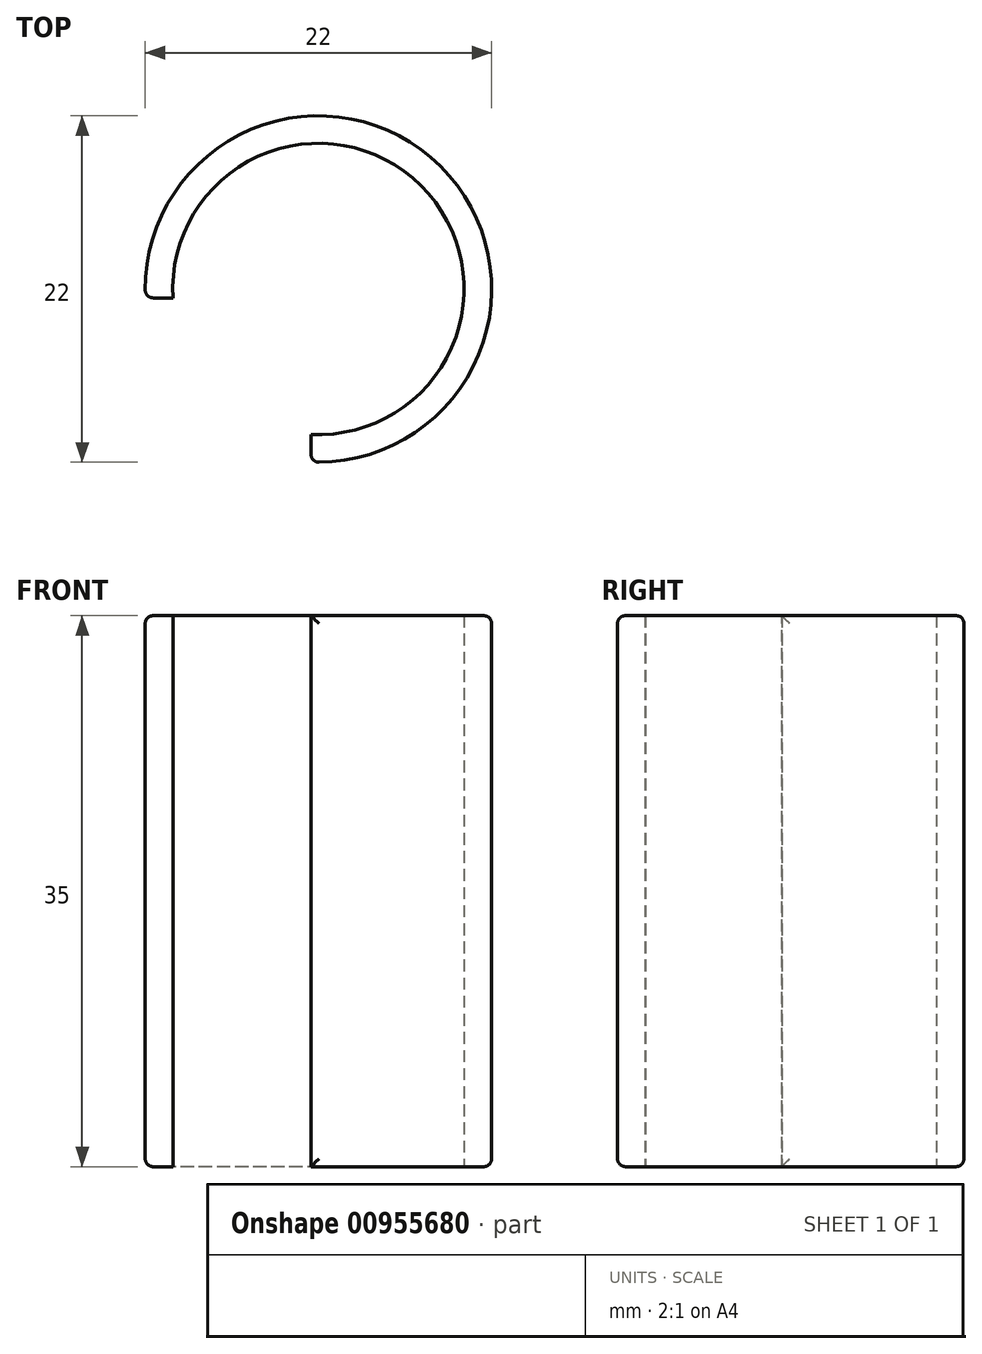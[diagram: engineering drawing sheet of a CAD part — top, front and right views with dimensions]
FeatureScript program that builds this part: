
annotation { "Feature Type Name" : "Feature", "Feature Type Description" : "" }
export const myFeature = defineFeature(function(context is Context, id is Id, definition is map)
    precondition{}
    {
        {
            var Q0;
            Q0=qCreatedBy(makeId("Top.planeOp"),FACE);
            var sketch = newSketch(context, id + "F0", { "sketchPlane" : qUnion([Q0])});
            skCircle(sketch, "E0", {"center": v(0, 0) * mm, "radius": 11 * mm});
            skSolve(sketch);
        }
        {
            var Q0;
            Q0=makeQuery(id+"F0.imprint","IMPRINT",FACE,{"disambiguationData":[TD([[makeQuery(id+"F0.imprint","IMPRINT",EDGE,{"derivedFrom":sQuery(id+"F0.wireOp",EDGE,"E0")}),1.0]])]});
            extrude(context, id + "F1", {"entities" : qUnion([Q0]), "depth" : 35 * mm, "offsetDistance" : 25 * mm});
        }
        {
            var Q0;
            Q0=qCreatedBy(makeId("Top.planeOp"),FACE);
            var sketch = newSketch(context, id + "F2", { "sketchPlane" : qUnion([Q0])});
            skCircle(sketch, "E1", {"center": v(0, 0) * mm, "radius": 9.25 * mm});
            skSolve(sketch);
        }
        {
            var Q0;
            Q0=makeQuery(id+"F2.imprint","IMPRINT",FACE,{"disambiguationData":[TD([[makeQuery(id+"F2.imprint","IMPRINT",EDGE,{"derivedFrom":sQuery(id+"F2.wireOp",EDGE,"E1")}),1.0]])]});
            extrude(context, id + "F3", {"entities" : qUnion([Q0]), "operationType" : NewBodyOperationType.REMOVE, "depth" : 60 * mm, "offsetDistance" : 25 * mm});
        }
        {
            var Q0;
            Q0=qCreatedBy(makeId("Top.planeOp"),FACE);
            var sketch = newSketch(context, id + "F4", { "sketchPlane" : qUnion([Q0])});
            skLineSegment(sketch, "E2.bottom", {"start": v(-0.47, -0.57) * mm, "end": v(-22.06, -0.57) * mm});
            skLineSegment(sketch, "E2.top", {"start": v(-0.47, -21.54) * mm, "end": v(-22.06, -21.54) * mm});
            skLineSegment(sketch, "E2.left", {"start": v(-0.47, -0.57) * mm, "end": v(-0.47, -21.54) * mm});
            skLineSegment(sketch, "E2.right", {"start": v(-22.06, -0.57) * mm, "end": v(-22.06, -21.54) * mm});
            skSolve(sketch);
        }
        {
            var Q0;
            Q0=qSketchRegion(id+"F4",true);
            extrude(context, id + "F5", {"entities" : qUnion([Q0]), "operationType" : NewBodyOperationType.REMOVE, "depth" : 60 * mm, "offsetDistance" : 25 * mm});
        }
        {
            var Q0;
            Q0=makeQuery(id+"F1.opExtrude","SWEPT_FACE",FACE,{"disambiguationData":[OSD([sQuery(id+"F0.wireOp",EDGE,"E0")])]});
            fillet(context, id + "F6", {"entities" : qUnion([Q0]), "radius" : 0.5 * mm, "tangentPropagation" : true, "allowEdgeOverflow" : false});
        }
    });
